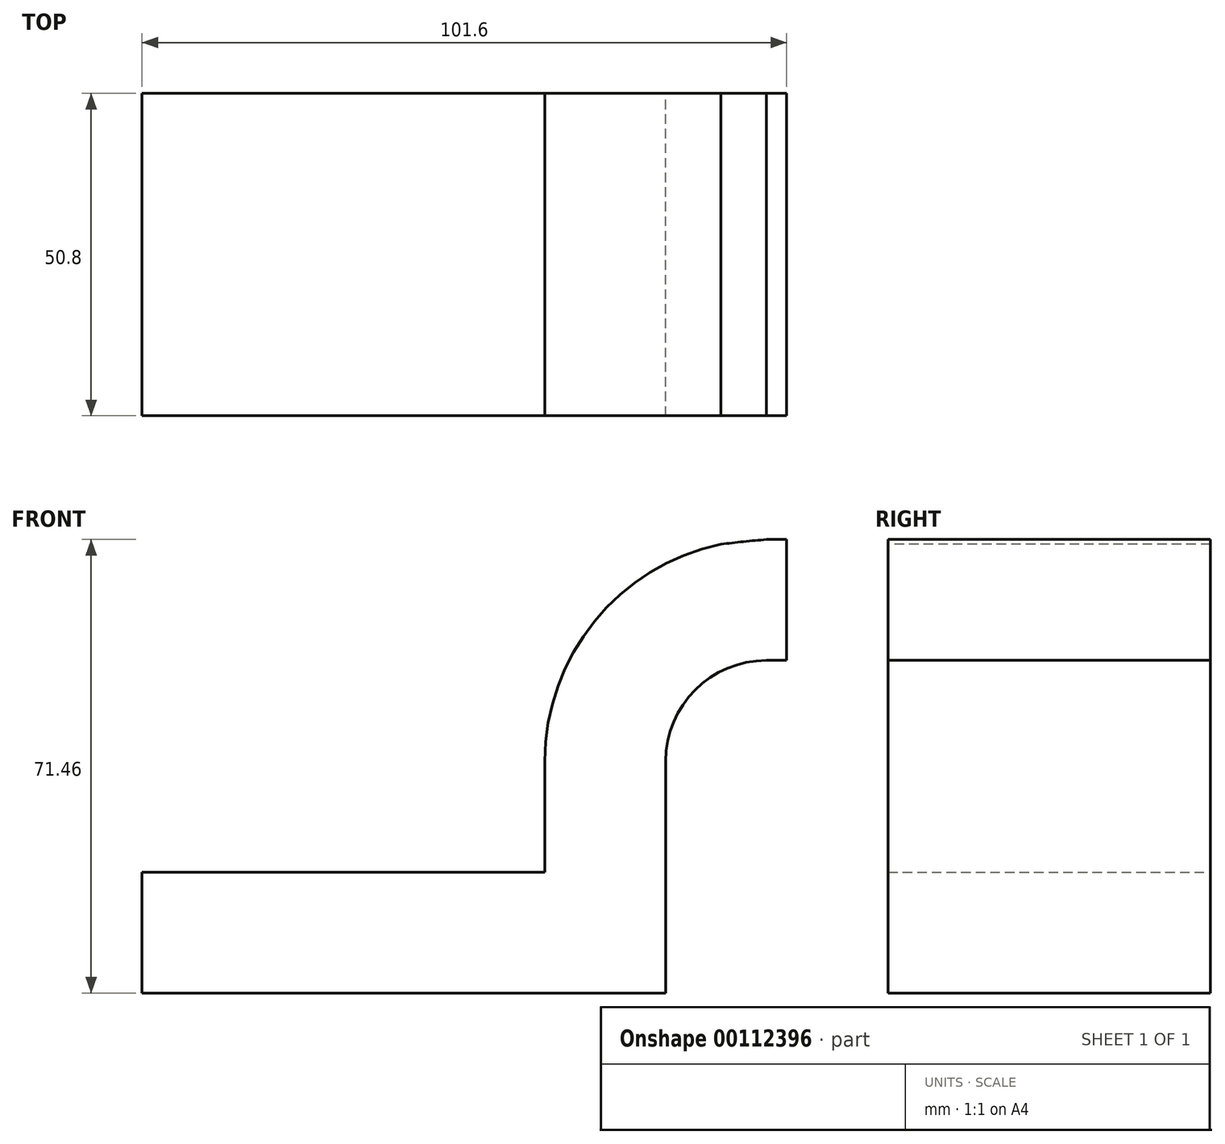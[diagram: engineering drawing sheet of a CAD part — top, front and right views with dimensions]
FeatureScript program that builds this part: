
annotation { "Feature Type Name" : "Feature", "Feature Type Description" : "" }
export const myFeature = defineFeature(function(context is Context, id is Id, definition is map)
    precondition{}
    {
        {
            var Q0;
            Q0=qCreatedBy(makeId("Front.planeOp"),FACE);
            var sketch = newSketch(context, id + "F0", { "sketchPlane" : qUnion([Q0])});
            skLineSegment(sketch, "E0.bottom", {"start": v(-41.28, 9.52) * mm, "end": v(41.28, 9.53) * mm});
            skLineSegment(sketch, "E0.top", {"start": v(-41.28, -9.53) * mm, "end": v(41.28, -9.53) * mm});
            skLineSegment(sketch, "E0.left", {"start": v(-41.28, 9.52) * mm, "end": v(-41.28, -9.53) * mm});
            skLineSegment(sketch, "E0.right", {"start": v(41.28, 9.53) * mm, "end": v(41.28, -9.52) * mm});
            skPoint(sketch, "E0.middle", {"position": v(0, 0) * mm});
            skLineSegment(sketch, "E1.bottom", {"start": v(60.32, 66.68) * mm, "end": v(111.12, 66.68) * mm});
            skLineSegment(sketch, "E1.top", {"start": v(60.33, 38.1) * mm, "end": v(111.12, 38.1) * mm});
            skLineSegment(sketch, "E1.left", {"start": v(60.32, 66.67) * mm, "end": v(60.32, 38.1) * mm});
            skLineSegment(sketch, "E1.right", {"start": v(111.12, 66.67) * mm, "end": v(111.12, 38.1) * mm});
            skPoint(sketch, "E1.middle", {"position": v(85.72, 52.39) * mm});
            skLineSegment(sketch, "E2", {"start": v(41.27, 9.53) * mm, "end": v(41.27, 27) * mm});
            skArc(sketch, "E3", {"start": v(41.27, 27) * mm, "mid": v(45.92, 38.23) * mm, "end": v(57.15, 42.88) * mm});
            skLineSegment(sketch, "E4", {"start": v(57.15, 42.88) * mm, "end": v(85.72, 42.88) * mm});
            skLineSegment(sketch, "E5.0", {"start": v(57.15, 61.93) * mm, "end": v(85.72, 61.93) * mm});
            skArc(sketch, "E5.1", {"start": v(22.23, 27) * mm, "mid": v(32.45, 51.7) * mm, "end": v(57.15, 61.93) * mm});
            skLineSegment(sketch, "E5.2", {"start": v(22.22, 9.53) * mm, "end": v(22.22, 27) * mm});
            skLineSegment(sketch, "E6", {"start": v(85.72, 38.1) * mm, "end": v(85.72, 66.68) * mm});
            skFitSpline(sketch, "E7", {"points": [v(57.15, 61.93) * mm, v(-41.28, 9.52) * mm], "startDerivative": vector(-119.25, -9.92) * mm, "endDerivative": vector(-62.21, -96.79) * mm});
            skSolve(sketch);
        }
        {
            var Q0;
            Q0=makeQuery(id+"F0.imprint","IMPRINT",FACE,{"disambiguationData":[TD([[makeQuery(id+"F0.imprint","IMPRINT",EDGE,{"derivedFrom":sQuery(id+"F0.wireOp",EDGE,"E0.top")}),1.0]])]});
            var Q1;
            {var subQ6=sQuery(id+"F0.wireOp",EDGE,"E2");Q1=makeQuery(id+"F0.imprint","IMPRINT",FACE,{"disambiguationData":[TD([[makeQuery(id+"F0.imprint","IMPRINT",EDGE,{"derivedFrom":subQ6}),1.0]])]});}
            extrude(context, id + "F1", {"entities" : qUnion([Q0, Q1]), "endBound" : BoundingType.SYMMETRIC, "depth" : 50.8 * mm});
        }
    });
